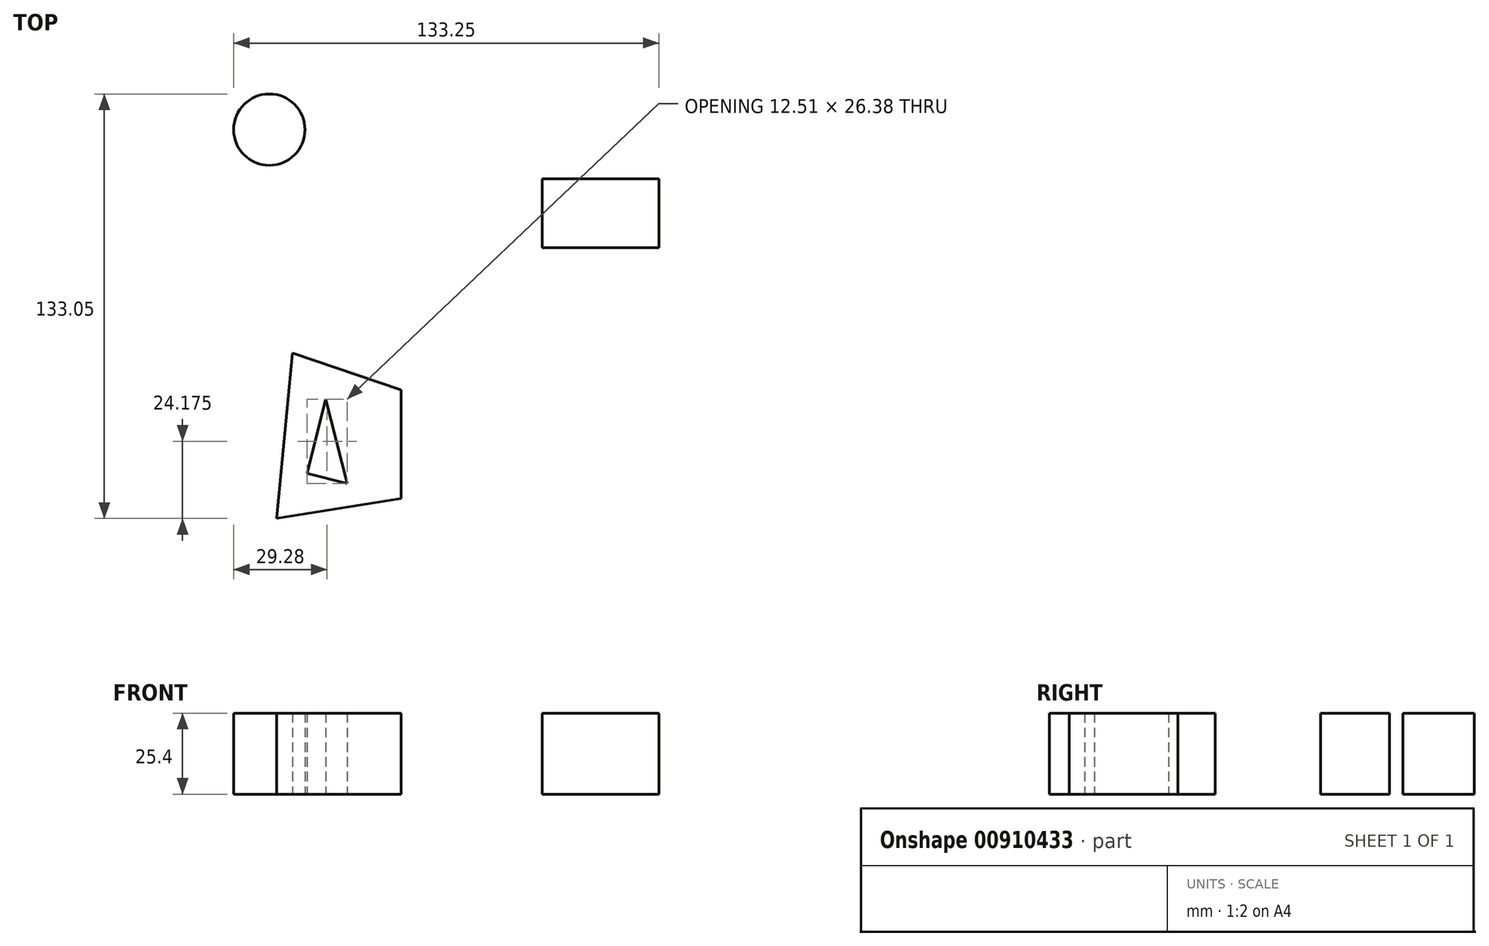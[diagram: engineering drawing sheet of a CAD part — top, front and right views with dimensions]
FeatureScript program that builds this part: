
annotation { "Feature Type Name" : "Feature", "Feature Type Description" : "" }
export const myFeature = defineFeature(function(context is Context, id is Id, definition is map)
    precondition{}
    {
        {
            var Q0;
            Q0=qCreatedBy(makeId("Top.planeOp"),FACE);
            var sketch = newSketch(context, id + "F0", { "sketchPlane" : qUnion([Q0])});
            skCircle(sketch, "E0", {"center": v(-62.28, 52.52) * mm, "radius": 11.18 * mm});
            skLineSegment(sketch, "E1.bottom", {"start": v(23.25, 37.16) * mm, "end": v(59.79, 37.16) * mm});
            skLineSegment(sketch, "E1.top", {"start": v(23.25, 15.57) * mm, "end": v(59.79, 15.57) * mm});
            skLineSegment(sketch, "E1.left", {"start": v(23.25, 37.16) * mm, "end": v(23.25, 15.57) * mm});
            skLineSegment(sketch, "E1.right", {"start": v(59.79, 37.16) * mm, "end": v(59.79, 15.57) * mm});
            skLineSegment(sketch, "E2", {"start": v(-55, -17.45) * mm, "end": v(-20.95, -29.08) * mm});
            skLineSegment(sketch, "E3", {"start": v(-20.95, -29.08) * mm, "end": v(-20.95, -63.13) * mm});
            skLineSegment(sketch, "E4", {"start": v(-20.95, -63.13) * mm, "end": v(-59.98, -69.35) * mm});
            skLineSegment(sketch, "E5", {"start": v(-59.98, -69.35) * mm, "end": v(-55, -17.45) * mm});
            skLineSegment(sketch, "E6", {"start": v(-44.62, -31.99) * mm, "end": v(-50.43, -55.24) * mm});
            skLineSegment(sketch, "E7", {"start": v(-50.43, -55.24) * mm, "end": v(-37.93, -58.36) * mm});
            skLineSegment(sketch, "E8", {"start": v(-37.93, -58.36) * mm, "end": v(-44.62, -31.99) * mm});
            skLineSegment(sketch, "E9", {"start": v(-82.91, 71.7) * mm, "end": v(-82.91, 30.26) * mm, "construction": true});
            skSolve(sketch);
        }
        {
            var Q0;
            Q0=makeQuery(id+"F0.imprint","IMPRINT",FACE,{"disambiguationData":[TD([[makeQuery(id+"F0.imprint","IMPRINT",EDGE,{"derivedFrom":sQuery(id+"F0.wireOp",EDGE,"E2")}),-1.0]])]});
            var Q1;
            Q1=makeQuery(id+"F0.imprint","IMPRINT",FACE,{"disambiguationData":[TD([[makeQuery(id+"F0.imprint","IMPRINT",EDGE,{"derivedFrom":sQuery(id+"F0.wireOp",EDGE,"E0")}),1.0]])]});
            var Q2;
            Q2=makeQuery(id+"F0.imprint","IMPRINT",FACE,{"disambiguationData":[TD([[makeQuery(id+"F0.imprint","IMPRINT",EDGE,{"derivedFrom":sQuery(id+"F0.wireOp",EDGE,"E1.bottom")}),-1.0]])]});
            extrude(context, id + "F1", {"entities" : qUnion([Q0, Q1, Q2]), "depth" : 25.4 * mm, "offsetDistance" : 25.4 * mm});
        }
    });
